# Revit family: PRD_AR_ShwrFttngsPckg_ShowerPanel_F5ST2020-29
name_source: partatom
category: Plumbing Fixtures
revit_build: Autodesk Revit 2018 (Build: 20190510_1515(x64)
units: mm (PartAtom-declared; Revit-internal decimal feet)

## family parameters
Cut with Voids When Loaded = No
Host = Face
OmniClass Number = 23.45.05.14.17
OmniClass Title = Showers
Part Type = Normal
Room Calculation Point = No
Round Connector Dimension = Use Diameter
Shared = No

## types (10) — shared parameters
AdditionalConnections = No
AdjustableFlowTime = Yes
AssetType = Fixed
CasingMaterial = PRD_AR_StainlessSteel_SatinFinished_Dark
Category = Pr_40_20_87_75, Shower fittings package
Circulation = No
ConnectionWithPayWaterDispenser = Not possible
Default Elevation = 1500 mm  [stored 4.92126 ft]
DurationUnit = year
FittingMaterial = PRD_AR_ChromatedBrass_HighPolished
FlowColdWater = 0.2 L/s
FlowHotWater = 0.2 L/s
FunctionalPrinciple = Hydraulic self-closing
IfcExportAs = IfcSanitaryTerminalType
IfcExportType = SHOWER
InletSize = G-1-2-A
Manufacturer = KWC Group AG
ManufacturerName = KWC Group AG
ManufacturerURL = www.kwc.com
MaximumFlowTime = 35.00 seconds
MinimumFlowTime = 5.00 seconds
NBSDescription = Shower fittings package
NBSReference = 45-35-70/330
NominalHeight = 1160 mm  [stored 3.80577 ft]
NominalWidth = 235 mm  [stored 0.770997 ft]
PositionOfWaterConnection = From top / backside
ProductInformation = https://pim.kwc.com
ProtectiveShutdown = No
ShowerType = Individual
SoundInsulation = No
TubeMaterial = PRD_AR_StainlessSteel_SatinFinished
TypeOfMixing = Thermostat
TypeOfMounting = Wall mounting
TypeOfOperation = Manual operation
TypeOfShower = Shower panel
URL = www.kwc.com
Uniclass2015Code = Pr_40_20_87_75
Uniclass2015Title = Shower fittings package
Uniclass2015Version = Products v1.17
Version = 1
WarrantyDurationUnit = year
zero-valued in all types: DrainSize

## per-type parameters (varying)
- F5ST2020: BIMObjectName=PRD_AR_ShowerFittingsPackage_ShowerPanel_F5ST2020; BodyMaterial=PRD_AR_StainlessSteel_SatinFinished; Color=stainless steel; ColorCasing=Yes; DefaultAutomaticHygieneFlushing=Fixed interval 24 hours; Description=F5S Therm shower panel made of stainless steel for wall mounting with DN 15 self-closing thermostatic mixer and connecting nozzles for the shower head. Hydraulically controlled, for connection to hot water and cold water. Shower valve with integrated FRAMIC self-closing cartridge, thermostat and pre-assembled hygiene unit including sensor with control electronics to perform automatic water hygiene flushing, program-controlled thermal disinfection (additional bypass solenoid-operated flush valve cartridge required) and storage of statistical data. FRAMIC self-closing cartridge, low maintenance and stagnation free, with ceramic disc technology, self closing, flow pressure independent due to the medium-independent design. Stepless adjustment of flow duration. Thermostat with metal handle, an adjustable and turn-proof temperature stop and an option for manual thermal disinfection. All-metal construction, visible parts high-polished or chrome-plated. Connecting nozzles for the required additional DN 15 KWC shower head with pre-fitted flow regulator 9.0 l/min. Housing made of stainless steel with raised function surface and plastic cover caps. Connecting hoses with lockable water volume control with backflow preventer and strainer. Activated water hygiene flushing at fixed intervals of 24 hours. With option for parameterization and communication via the optional bidirectional remote control. Optional hygiene unit for battery operation with 6 V lithium battery (CR-P2) per fitting or separate power supply via plug-in power supply unit 6.75 V/12 V DC.; Features=stainless steel, with self-closing thermostatic mixer; Finish=satin finished; GrossWeight=10.20 kg; HandShowerFittingOffset=0 mm  [stored 0 ft]; HandShowerVisibility=No; HasTray=No; HygieneFlushing=Yes; IntegralAccessories=shower head and battery compartment including battery or plug-in power supply unit with extension cable to be ordered separately; Material=stainless steel; MaterialCode=1.4301; MinimumFlowPressure=1.50 bar; ModelNumber=2030055929; Name=Shower Panel F5ST2020; NetWeight=9.00 kg; NominalDepth=90 mm  [stored 0.295276 ft]; PositionOfPowerConnection=Top backside; PowerConsumption=1.5; PowerSupplyConnection=6-12-VDC; ProtectiveSystemIP=IP 59K; ShelfVisibility=No; ShowerPipeDraining=No; Size=235 x 1160 x 90 mm (W x H x D); TailorMade=No; ThermalDisinfection=Prepared for automatic thermal disinfection; TypeOfSensor=Opto-electronic sensor; VolumeFlowRate=0.15 L/s at 3 bar
- F5ST2021: BIMObjectName=PRD_AR_ShowerFittingsPackage_ShowerPanel_F5ST2021; BodyMaterial=PRD_AR_StainlessSteel_SatinFinished; Color=stainless steel; ColorCasing=Yes; DefaultAutomaticHygieneFlushing=Fixed interval 24 hours; Description=F5S Therm shower panel made of stainless steel for wall mounting with DN 15 self-closing thermostatic mixer and a hand shower fitting. Hydraulically controlled, for connection to hot water and cold water. Shower valve with integrated FRAMIC self-closing cartridge, thermostat and pre-assembled hygiene unit including sensor with control electronics to perform automatic water hygiene flushing, program-controlled thermal disinfection (additional bypass solenoid-operated flush valve cartridge required) and storage of statistical data. FRAMIC self-closing cartridge, low maintenance and stagnation free, with ceramic disc technology, self closing, flow pressure independent due to the medium-independent design. Stepless adjustment of flow duration. Thermostat with metal handle, an adjustable and turn-proof temperature stop and an option for manual thermal disinfection. All-metal construction, visible parts high-polished or chrome-plated. Pre-fitted chrome-plated brass shower pole with height-adjustable hand shower holder and chrome-plated plastic hand shower, shower head with rain jet, diameter 110 mm, shower hose 900 mm. Housing made of stainless steel with raised function surface and plastic cover caps. Connecting hoses with lockable water volume control with backflow preventer and strainer. Activated water hygiene flushing at fixed intervals of 24 hours. With option for parameterization and communication via the optional bidirectional remote control. Optional hygiene unit for battery operation with 6 V lithium battery (CR-P2) per fitting or separate power supply via plug-in power supply unit 6.75 V/12 V DC.; Features=stainless steel, with self-closing thermostatic mixer and a hand shower fitting; Finish=satin finished; GrossWeight=11.30 kg; HandShowerFittingOffset=0 mm  [stored 0 ft]; HandShowerVisibility=Yes; HasTray=No; HygieneFlushing=Yes; IntegralAccessories=battery compartment including battery or plug-in power supply unit with extension cable to be ordered separately; Material=stainless steel; MaterialCode=1.4301; MinimumFlowPressure=1.00 bar; ModelNumber=2030056539; Name=Shower Panel F5ST2021; NetWeight=10.74 kg; NominalDepth=90 mm  [stored 0.295276 ft]; PositionOfPowerConnection=Top backside; PowerConsumption=1.5; PowerSupplyConnection=6-12-VDC; ProtectiveSystemIP=IP 59K; ShelfVisibility=No; ShowerPipeDraining=No; Size=235 x 1160 x 90 mm (W x H x D); TailorMade=No; ThermalDisinfection=Prepared for automatic thermal disinfection; TypeOfSensor=Opto-electronic sensor
- F5ST2022: BIMObjectName=PRD_AR_ShowerFittingsPackage_ShowerPanel_F5ST2022; BodyMaterial=PRD_AR_StainlessSteel_SatinFinished; Color=stainless steel; ColorCasing=Yes; Description=F5S Therm shower panel made of stainless steel for wall mounting with DN 15 self-closing thermostatic mixer and connecting nozzles for the shower head. Hydraulically controlled, for connection to hot water and cold water. Shower valve with integrated FRAMIC self-closing cartridge, thermostat and mechanism for an optional water hygiene unit for automatic water hygiene flushing, program-controlled thermal disinfection (additional bypass solenoid-operated flush valve cartridge required) and storage of statistical data. FRAMIC self-closing cartridge, low maintenance and stagnation free, with ceramic disc technology, self closing, flow pressure independent due to the medium-independent design. Stepless adjustment of flow duration. Thermostat with metal handle, an adjustable and turn-proof temperature stop and an option for manual thermal disinfection. All-metal construction, visible parts high-polished or chrome-plated. Connecting nozzles for the required additional DN 15 KWC shower head with pre-fitted flow regulator 9.0 l/min. Housing made of stainless steel with raised function surface and plastic cover caps. Connecting hoses with lockable water volume control with backflow preventer and strainer.; Features=stainless steel, with self-closing thermostatic mixer; Finish=satin finished; GrossWeight=12.00 kg; HandShowerFittingOffset=0 mm  [stored 0 ft]; HandShowerVisibility=No; HasTray=No; HygieneFlushing=Prepared; IntegralAccessories=shower head to be ordered separately; Material=stainless steel; MaterialCode=1.4301; MinimumFlowPressure=1.50 bar; ModelNumber=2030056541; Name=Shower Panel F5ST2022; NetWeight=10.15 kg; NominalDepth=90 mm  [stored 0.295276 ft]; ShelfVisibility=No; ShowerPipeDraining=No; Size=235 x 1160 x 90 mm (W x H x D); TailorMade=No; ThermalDisinfection=Automatic; VolumeFlowRate=0.15 L/s at 3 bar
- F5ST2023: BIMObjectName=PRD_AR_ShowerFittingsPackage_ShowerPanel_F5ST2023; BodyMaterial=PRD_AR_StainlessSteel_SatinFinished; Color=stainless steel; ColorCasing=Yes; Description=F5S Therm shower panel made of stainless steel for wall mounting with DN 15 self-closing thermostatic mixer and a hand shower fitting. Hydraulically controlled, for connection to hot water and cold water. Shower valve with integrated FRAMIC self-closing cartridge, thermostat and mechanism for an optional water hygiene unit for automatic water hygiene flushing, program-controlled thermal disinfection (additional bypass solenoid-operated flush valve cartridge required) and storage of statistical data. FRAMIC self-closing cartridge, low maintenance and stagnation free, with ceramic disc technology, self closing, flow pressure independent due to the medium-independent design. Stepless adjustment of flow duration. Thermostat with metal handle, an adjustable and turn-proof temperature stop and an option for manual thermal disinfection. All-metal construction, visible parts high-polished or chrome-plated. Pre-fitted chrome-plated brass shower pole with height-adjustable hand shower holder and chrome-plated plastic hand shower, shower head with rain jet, diameter 110 mm, shower hose 900 mm. Housing made of stainless steel with raised function surface and plastic cover caps. Connecting hoses with lockable water volume control with backflow preventer and strainer.; Features=stainless steel, with self-closing thermostatic mixer and a hand shower fitting; Finish=satin finished; GrossWeight=14.00 kg; HandShowerFittingOffset=0 mm  [stored 0 ft]; HandShowerVisibility=Yes; HasTray=No; HygieneFlushing=Prepared; Material=stainless steel; MaterialCode=1.4301; MinimumFlowPressure=1.00 bar; ModelNumber=2030056542; Name=Shower Panel F5ST2023; NetWeight=12.00 kg; NominalDepth=90 mm  [stored 0.295276 ft]; ShelfVisibility=No; ShowerPipeDraining=No; Size=235 x 1160 x 90 mm (W x H x D); TailorMade=No; ThermalDisinfection=Prepared for automatic thermal disinfection
- F5ST2024: BIMObjectName=PRD_AR_ShowerFittingsPackage_ShowerPanel_F5ST2024; BodyMaterial=PRD_AR_MineralMaterial_Chromed; Color=alpine white; ColorCasing=No; DefaultAutomaticHygieneFlushing=Fixed interval 24 hours; Description=F5S Therm shower panel made of mineral material for wall mounting with DN 15 self-closing thermostatic mixer and connecting nozzles for the shower head. Hydraulically controlled, for connection to hot water and cold water. Shower valve with integrated FRAMIC self-closing cartridge, thermostat and pre-assembled hygiene unit including sensor with control electronics to perform automatic water hygiene flushing, program-controlled thermal disinfection (additional bypass solenoid-operated flush valve cartridge required) and storage of statistical data. FRAMIC self-closing cartridge, low maintenance and stagnation free, with ceramic disc technology, self closing, flow pressure independent due to the medium-independent design. Stepless adjustment of flow duration. Thermostat with metal handle, an adjustable and turn-proof temperature stop and an option for manual thermal disinfection. All-metal construction, visible parts high-polished or chrome-plated. Connecting nozzles for the required additional DN 15 KWC shower head with pre-fitted flow regulator 9.0 l/min. Housing with raised function surface made of MIRANIT resin-bonded mineral material with pore-free smooth surface (temperature-resistant up to 80°C), Alpine white colour. Connecting hoses with lockable water volume control with backflow preventer and strainer. Activated water hygiene flushing at fixed intervals of 24 hours. With option for parameterization and communication via the optional bidirectional remote control. Optional hygiene unit for battery operation with 6 V lithium battery (CR-P2) per fitting or separate power supply via plug-in power supply unit 6.75 V/12 V DC.; Features=mineral material, with self-closing thermostatic mixer; Finish=chromed; GrossWeight=16.50 kg; HandShowerFittingOffset=10 mm  [stored 0.0328084 ft]; HandShowerVisibility=No; HasTray=No; HygieneFlushing=Yes; IntegralAccessories=shower head and battery compartment including battery or plug-in power supply unit with extension cable to be ordered separately; Material=mineral material; MaterialCode=Miranit; MinimumFlowPressure=1.50 bar; ModelNumber=2030056543; Name=Shower Panel F5ST2024; NetWeight=15.00 kg; NominalDepth=100 mm  [stored 0.328084 ft]; PositionOfPowerConnection=Top backside; PowerConsumption=1.5; PowerSupplyConnection=6-12-VDC; ProtectiveSystemIP=IP 59K; ShelfVisibility=No; ShowerPipeDraining=No; Size=235 x 1160 x 100 mm (W x H x D); TailorMade=No; ThermalDisinfection=Prepared for automatic thermal disinfection; TypeOfSensor=Opto-electronic sensor; VolumeFlowRate=0.15 L/s at 3 bar
- F5ST2025: BIMObjectName=PRD_AR_ShowerFittingsPackage_ShowerPanel_F5ST2025; BodyMaterial=PRD_AR_MineralMaterial_Chromed; Color=alpine white; ColorCasing=No; DefaultAutomaticHygieneFlushing=Fixed interval 24 hours; Description=F5S Therm shower panel made of mineral material for wall mounting with DN 15 self-closing thermostatic mixer and a hand shower fitting. Hydraulically controlled, for connection to hot water and cold water. Shower valve with integrated FRAMIC self-closing cartridge, thermostat and pre-assembled hygiene unit including sensor with control electronics to perform automatic water hygiene flushing, program-controlled thermal disinfection (additional bypass solenoid-operated flush valve cartridge required) and storage of statistical data. FRAMIC self-closing cartridge, low maintenance and stagnation free, with ceramic disc technology, self closing, flow pressure independent due to the medium-independent design. Stepless adjustment of flow duration. Thermostat with metal handle, an adjustable and turn-proof temperature stop and an option for manual thermal disinfection. All-metal construction, visible parts high-polished or chrome-plated. Pre-fitted chrome-plated brass shower pole with height-adjustable hand shower holder and chrome-plated plastic hand shower, shower head with rain jet, diameter 110 mm, shower hose 900 mm. Housing with raised function surface made of MIRANIT resin-bonded mineral material with pore-free smooth surface (temperature-resistant up to 80°C), Alpine white colour. Connecting hoses with lockable water volume control with backflow preventer and strainer. Activated water hygiene flushing at fixed intervals of 24 hours. With option for parameterization and communication via the optional bidirectional remote control. Optional hygiene unit for battery operation with 6 V lithium battery (CR-P2) per fitting or separate power supply via plug-in power supply unit 6.75 V/12 V DC.; Features=mineral material, with self-closing thermostatic mixer and a hand shower fitting; Finish=chromed; GrossWeight=16.50 kg; HandShowerFittingOffset=10 mm  [stored 0.0328084 ft]; HandShowerVisibility=Yes; HasTray=No; HygieneFlushing=Yes; IntegralAccessories=battery compartment including battery or plug-in power supply unit with extension cable to be ordered separately; Material=mineral material; MaterialCode=Miranit; MinimumFlowPressure=1.00 bar; ModelNumber=2030056544; Name=Shower Panel F5ST2025; NetWeight=15.00 kg; NominalDepth=100 mm  [stored 0.328084 ft]; PositionOfPowerConnection=Top backside; PowerConsumption=1.5; PowerSupplyConnection=6-12-VDC; ProtectiveSystemIP=IP 59K; ShelfVisibility=No; ShowerPipeDraining=No; Size=235 x 1160 x 100 mm (W x H x D); TailorMade=No; ThermalDisinfection=Prepared for automatic thermal disinfection; TypeOfSensor=Opto-electronic sensor
- F5ST2026: BIMObjectName=PRD_AR_ShowerFittingsPackage_ShowerPanel_F5ST2026; BodyMaterial=PRD_AR_MineralMaterial_Chromed; Color=alpine white; ColorCasing=No; DefaultAutomaticHygieneFlushing=Fixed interval 24 hours; Description=F5S Therm shower panel made of mineral material for wall mounting with DN 15 self-closing thermostatic mixer and connecting nozzles for the shower head. Hydraulically controlled, for connection to hot water and cold water. Shower valve with integrated FRAMIC self-closing cartridge, thermostat and pre-assembled hygiene unit including sensor with control electronics to perform automatic water hygiene flushing, program-controlled thermal disinfection (additional bypass solenoid-operated flush valve cartridge required) and storage of statistical data. FRAMIC self-closing cartridge, low maintenance and stagnation free, with ceramic disc technology, self closing, flow pressure independent due to the medium-independent design. Stepless adjustment of flow duration. Thermostat with metal handle, an adjustable and turn-proof temperature stop and an option for manual thermal disinfection. All-metal construction, visible parts high-polished or chrome-plated. Connecting nozzles for the required additional DN 15 KWC shower head with pre-fitted flow regulator 9.0 l/min. Housing with raised function surface and seamless moulded shower gel shelf made of MIRANIT resin-bonded mineral material with pore-free smooth surface (temperature-resistant up to 80°C), Alpine white colour. Connecting hoses with lockable water volume control with backflow preventer and strainer. Activated water hygiene flushing at fixed intervals of 24 hours. With option for parameterization and communication via the optional bidirectional remote control. Optional hygiene unit for battery operation with 6 V lithium battery (CR-P2) per fitting or separate power supply via plug-in power supply unit 6.75 V/12 V DC.; Features=mineral material, with self-closing thermostatic mixer; Finish=chromed; GrossWeight=14.00 kg; HandShowerFittingOffset=10 mm  [stored 0.0328084 ft]; HandShowerVisibility=No; HasTray=Yes; HygieneFlushing=Yes; IntegralAccessories=battery compartment including battery or plug-in power supply unit with extension cable to be ordered separately; Material=mineral material; MaterialCode=Miranit; MinimumFlowPressure=1.50 bar; ModelNumber=2030054253; Name=Shower Panel F5ST2026; NetWeight=13.30 kg; NominalDepth=100 mm  [stored 0.328084 ft]; PositionOfPowerConnection=Top backside; PowerConsumption=1.5; PowerSupplyConnection=6-12-VDC; ProtectiveSystemIP=IP 59K; ShelfVisibility=Yes; ShowerPipeDraining=No; Size=235 x 1160 x 100 mm (W x H x D); ThermalDisinfection=Prepared for automatic thermal disinfection; TypeOfSensor=Opto-electronic sensor; VolumeFlowRate=0.15 L/s at 3 bar
- F5ST2027: BIMObjectName=PRD_AR_ShowerFittingsPackage_ShowerPanel_F5ST2027; BodyMaterial=PRD_AR_MineralMaterial_Chromed; Color=alpine white; ColorCasing=No; Description=F5S Therm shower panel made of mineral material for wall mounting with DN 15 self-closing thermostatic mixer and connecting nozzles for the shower head. Hydraulically controlled, for connection to hot water and cold water. Shower valve with integrated FRAMIC self-closing cartridge, thermostat and mechanism for an optional water hygiene unit for automatic water hygiene flushing, program-controlled thermal disinfection (additional bypass solenoid-operated flush valve cartridge required) and storage of statistical data. FRAMIC self-closing cartridge, low maintenance and stagnation free, with ceramic disc technology, self closing, flow pressure independent due to the medium-independent design. Stepless adjustment of flow duration. Thermostat with metal handle, an adjustable and turn-proof temperature stop and an option for manual thermal disinfection. All-metal construction, visible parts high-polished or chrome-plated. Connecting nozzles for the required additional DN 15 KWC shower head with pre-fitted flow regulator 9.0 l/min. Housing with raised function surface made of MIRANIT resin-bonded mineral material with pore-free smooth surface (temperature-resistant up to 80°C), Alpine white colour. Connecting hoses with lockable water volume control with backflow preventer and strainer.; Features=mineral material, with self-closing thermostatic mixer; Finish=chromed; GrossWeight=13.05 kg; HandShowerFittingOffset=10 mm  [stored 0.0328084 ft]; HandShowerVisibility=No; HasTray=No; HygieneFlushing=Prepared; IntegralAccessories=shower head to be ordered separately; Material=mineral material; MaterialCode=Miranit; MinimumFlowPressure=1.50 bar; ModelNumber=2030056545; Name=Shower Panel F5ST2027; NetWeight=12.40 kg; NominalDepth=100 mm  [stored 0.328084 ft]; ShelfVisibility=No; ShowerPipeDraining=No; Size=235 x 1160 x 100 mm (W x H x D); TailorMade=No; ThermalDisinfection=Prepared for automatic thermal disinfection; VolumeFlowRate=0.15 L/s at 3 bar
- F5ST2028: BIMObjectName=PRD_AR_ShowerFittingsPackage_ShowerPanel_F5ST2028; BodyMaterial=PRD_AR_MineralMaterial_Chromed; Color=alpine white; ColorCasing=No; Description=F5S Therm shower panel made of mineral material for wall mounting with DN 15 self-closing thermostatic mixer and a hand shower fitting. Hydraulically controlled, for connection to hot water and cold water. Shower valve with integrated FRAMIC self-closing cartridge, thermostat and mechanism for an optional water hygiene unit for automatic water hygiene flushing, program-controlled thermal disinfection (additional bypass solenoid-operated flush valve cartridge required) and storage of statistical data. FRAMIC self-closing cartridge, low maintenance and stagnation free, with ceramic disc technology, self closing, flow pressure independent due to the medium-independent design. Stepless adjustment of flow duration. Thermostat with metal handle, an adjustable and turn-proof temperature stop and an option for manual thermal disinfection. All-metal construction, visible parts high-polished or chrome-plated. Pre-fitted chrome-plated brass shower pole with height-adjustable hand shower holder and chrome-plated plastic hand shower, shower head with rain jet, diameter 110 mm, shower hose 900 mm. Housing with raised function surface made of MIRANIT resin-bonded mineral material with pore-free smooth surface (temperature-resistant up to 80°C), Alpine white colour. Connecting hoses with lockable water volume control with backflow preventer and strainer.; Features=mineral material, with self-closing thermostatic mixer and a hand shower fitting; Finish=chromed; GrossWeight=16.50 kg; HandShowerFittingOffset=10 mm  [stored 0.0328084 ft]; HandShowerVisibility=Yes; HasTray=No; HygieneFlushing=Prepared; Material=mineral material; MaterialCode=Miranit; MinimumFlowPressure=1.00 bar; ModelNumber=2030056546; Name=Shower Panel F5ST2028; NetWeight=15.00 kg; NominalDepth=100 mm  [stored 0.328084 ft]; ShelfVisibility=No; ShowerPipeDraining=No; Size=235 x 1160 x 100 mm (W x H x D); TailorMade=No; ThermalDisinfection=Prepared for automatic thermal disinfection
- F5ST2029: BIMObjectName=PRD_AR_ShowerFittingsPackage_ShowerPanel_F5ST2029; BodyMaterial=PRD_AR_MineralMaterial_Chromed; Color=alpine white; ColorCasing=No; Description=F5S Therm shower panel made of mineral material for wall mounting with DN 15 self-closing thermostatic mixer and connecting nozzles for the shower head. Hydraulically controlled, for connection to hot water and cold water. Shower valve with integrated FRAMIC self-closing cartridge, thermostat and mechanism for an optional water hygiene unit for automatic water hygiene flushing, program-controlled thermal disinfection (additional bypass solenoid-operated flush valve cartridge required) and storage of statistical data. FRAMIC self-closing cartridge, low maintenance and stagnation free, with ceramic disc technology, self closing, flow pressure independent due to the medium-independent design. Stepless adjustment of flow duration. Thermostat with metal handle, an adjustable and turn-proof temperature stop and an option for manual thermal disinfection. All-metal construction, visible parts high-polished or chrome-plated. Connecting nozzles for the required additional DN 15 KWC shower head with pre-fitted flow regulator 9.0 l/min. Housing with raised function surface and seamless moulded shower gel shelf made of MIRANIT resin-bonded mineral material with pore-free smooth surface (temperature-resistant up to 80°C), Alpine white colour. Connecting hoses with lockable water volume control with backflow preventer and strainer.; Features=mineral material, with self-closing thermostatic mixer; Finish=chromed; GrossWeight=14.00 kg; HandShowerFittingOffset=10 mm  [stored 0.0328084 ft]; HandShowerVisibility=No; HasTray=Yes; HygieneFlushing=Prepared; IntegralAccessories=shower head to be ordered separately; Material=mineral material; MaterialCode=Miranit; MinimumFlowPressure=1.50 bar; ModelNumber=2030056547; Name=Shower Panel F5ST2029; NetWeight=13.00 kg; NominalDepth=100 mm  [stored 0.328084 ft]; ShelfVisibility=Yes; Size=235 x 1160 x 100 mm (W x H x D); TailorMade=No; ThermalDisinfection=Prepared for automatic thermal disinfection; VolumeFlowRate=0.15 L/s at 3 bar

note: column(s) folded — value = type name in every type: Model, ModelReference

note: [stored X ft] marks values corroborated as IEEE doubles in the binary element streams (Revit-internal decimal feet)

## geometry (parser evidence)
native form markers: Extrusion x1, Sweep x4
no freeform markers — native parametric forms only
